# Revit family: Air_Conditioner_Packaged_Rooftop Z(F,H,S,U) 6.5-7.5T_ Z(H,J,R,T,U,W,K,V) 3T-5T
name_source: partatom
category: Mechanical Equipment
revit_build: Autodesk Revit 2018 (Build: 20170630_0700(x64)
units: mm (PartAtom-declared; Revit-internal decimal feet)

## family parameters
Always vertical = Yes
Cut with Voids When Loaded = No
Part Type = Normal
Room Calculation Point = No
Round Connector Dimension = Use Radius
Shared = No
Work Plane-Based = No

## types (1)
- 3-10 Ton - Gas Heat
    Assembly Code = D3060300
    CTRL Bottom Return Center = 20 9/16"
    CTRL Bottom Supply Center = 18 13/16"
    Clearance Back = 36"
    Clearance Front = 36"
    Clearance Left = 36"
    Clearance Right = 12"
    Clearance Top = 72"
    Compressor Locked Rotor Current = 0 A
    Compressor Maximum Continuous Current = 0 A
    Compressor Quantity = 2
    Compressor Running Load Current = 0 A
    Compressor Type = Recip
    Condensate Drain Connection Description = Condensate Drain Connection
    Condensate Drain Connection Diameter = 1"
    Condensate Drain Connection Radius = 0"
    Condenser Coil Fins per Inch = 20
    Condenser Coils System One Rows = 0
    Condenser Coils System Two Rows = 0
    Condenser Fan Diameter = 24"
    Condenser Fan Quantity = 2
    Condenser Fan Type = Propeller
    Controls Connection Description = Control Wiring Connection
    Convenience Outlet Electrical Connection Description = Convenience Power Wiring Connection
    Convenience Outlet Full Load Current = 0 A
    Curb Length = 80 5/8"
    Curb Material = Metal - JCI - Steel - Galvanized With Wood Nailer
    Curb Width = 50 1/2"
    Description = Air Handling Unit, Commercial Comfort Systems, Series 10, Gas, 3-10 Ton Unit
    Economizer Hood Depth = 26"
    Economizer Hood Height = 18 7/8"
    Economizer Hood Length = 30 11/32"
    Electrical Connection Description = Power Wiring Connection
    Energy Efficiency Rating = 0
    Evaporator Coil Fins per Inch = 15
    Evaporator Coil Row Count = 3
    Family Revision Date = 06/11/2010
    Frame Finish = Paint - JCI - Powder Coated - Champagne
    Frame Material = Metal - JCI - Steel - Galvanized With Wood Nailer
    Frequency = 60 Hz
    Gas Connection Description = Gas Supply Connection
    Gas Connection Diameter = 1"
    Gas Connection Radius = 0"
    Height = 42"
    Integrated Part Load Value = 0
    Keynote = 15700
    Length = 89"
    Manufacturer = Johnson Controls, Inc.
    Maximum Applied Voltage = 0 V
    Maximum Overcurrent Protection = 0 A
    Minimum Applied Voltage = 0 V
    Minimum Circuit Current = 0 A
    Model = JA3ZHA2
    Nominal Air Flow = 0 CFM
    Nominal Cooling Capacity = 0.0 ton
    Number of Poles = 3
    OD Fan Motor Full Load Current = 0 A
    OmniClass Number = 23.75.10.24.21.27.11
    OmniClass Title = Packaged Air Conditioners
    Operating Weight = 0.00 lb
    Power Exhaust Full Load Current = 0 A
    Power Factor = 1
    Product Page URL = http://www.johnsoncontrols.com
    Refrigerant Charge System One = 0.00 lb
    Refrigerant Charge System Two = 0.00 lb
    Return Air Connection Description = Return Air Connection
    Seasonal Energy Efficiency Rating = 80
    Supply Air Connection Description = Supply Air Connection
    Supply Fan Full Load Current = 0 A
    URL = http://www.johnsoncontrols.com
    Voltage = 0 V
    Width = 59"

## geometry (parser evidence)
native form markers: Sweep x14
no freeform markers — native parametric forms only
